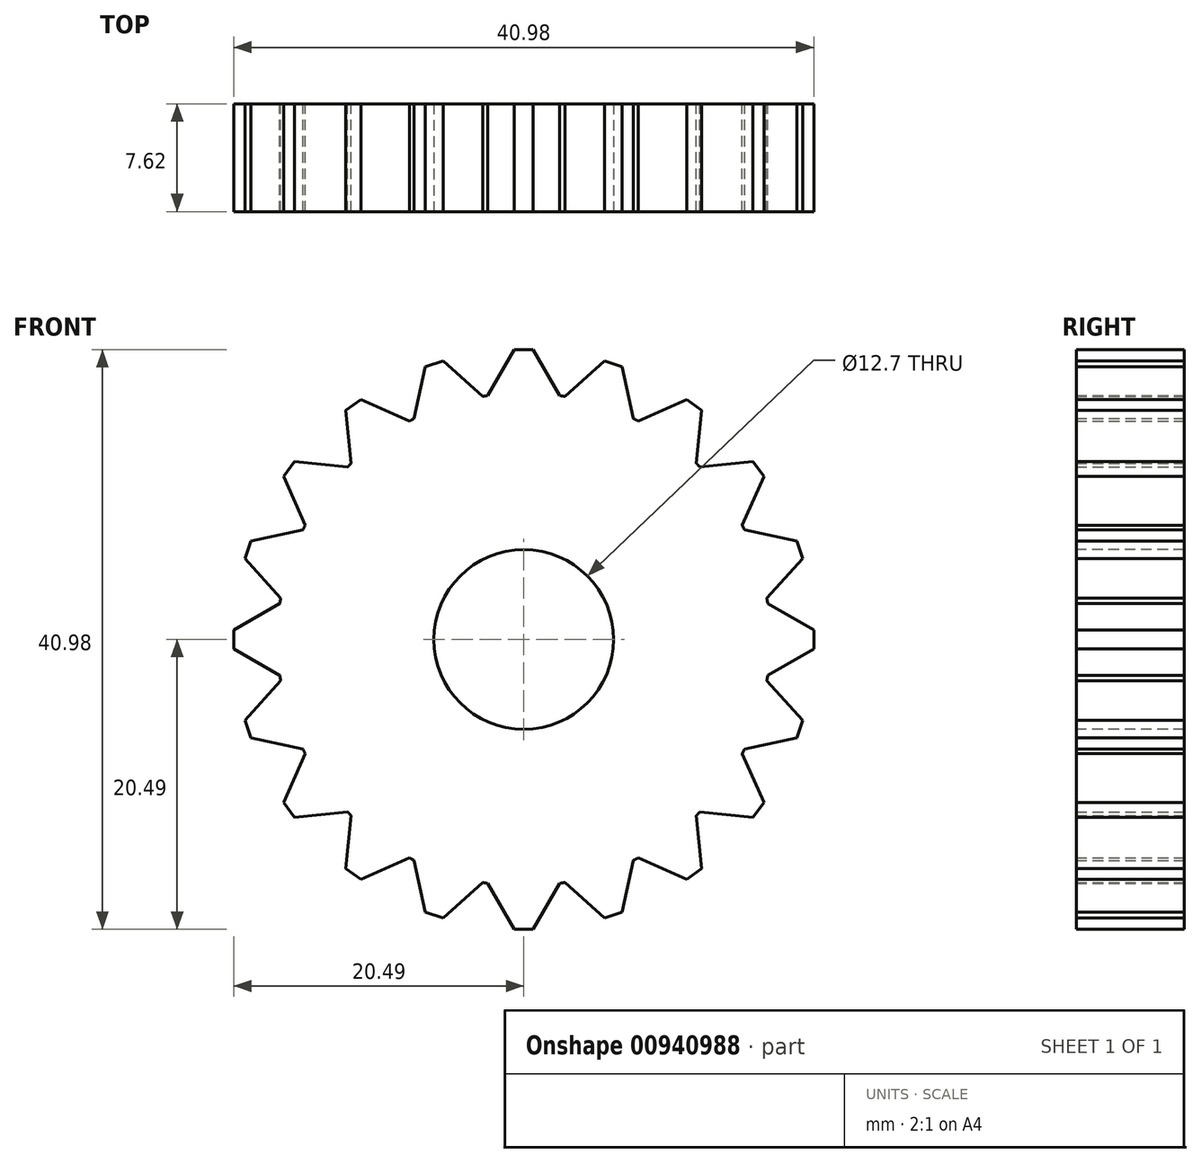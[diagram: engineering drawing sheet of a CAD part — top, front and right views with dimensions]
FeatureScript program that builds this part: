
annotation { "Feature Type Name" : "Feature", "Feature Type Description" : "" }
export const myFeature = defineFeature(function(context is Context, id is Id, definition is map)
    precondition{}
    {
        {
            var Q0;
            Q0=qCreatedBy(makeId("Front.planeOp"),FACE);
            var sketch = newSketch(context, id + "F0", { "sketchPlane" : qUnion([Q0])});
            skCircle(sketch, "E0", {"center": v(0, 0) * mm, "radius": 17.42 * mm});
            skSolve(sketch);
        }
        {
            var Q0;
            Q0=qSketchRegion(id+"F0",true);
            extrude(context, id + "F1", {"entities" : qUnion([Q0]), "depth" : 7.62 * mm, "offsetDistance" : 25.4 * mm});
        }
        {
            var Q0;
            Q0=makeQuery(id+"F1.opExtrude","CAP_FACE",FACE,{"disambiguationData":[OSD([sQuery(id+"F0.wireOp",EDGE,"E0")])],"isStart":true});
            var sketch = newSketch(context, id + "F2", { "sketchPlane" : qUnion([Q0])});
            skCircle(sketch, "E1.cCircle", {"center": v(-18.7, 0) * mm, "radius": 1.47 * mm, "construction": true});
            skLineSegment(sketch, "E1.0", {"start": v(-17.24, 2.54) * mm, "end": v(-17.24, -2.54) * mm});
            skLineSegment(sketch, "E1.1", {"start": v(-17.24, -2.54) * mm, "end": v(-21.63, 0) * mm});
            skLineSegment(sketch, "E1.2", {"start": v(-21.63, 0) * mm, "end": v(-17.24, 2.54) * mm});
            skPoint(sketch, "E1.0.midPoint", {"position": v(-17.24, 0) * mm});
            skLineSegment(sketch, "E2.1.0", {"start": v(-15.6, -7.74) * mm, "end": v(-20.58, -6.69) * mm});
            skLineSegment(sketch, "E2.1.1", {"start": v(-17.18, -2.91) * mm, "end": v(-15.6, -7.74) * mm});
            skLineSegment(sketch, "E2.1.2", {"start": v(-20.58, -6.69) * mm, "end": v(-17.18, -2.91) * mm});
            skLineSegment(sketch, "E2.2.0", {"start": v(-12.45, -12.19) * mm, "end": v(-17.5, -12.72) * mm});
            skLineSegment(sketch, "E2.2.1", {"start": v(-15.44, -8.08) * mm, "end": v(-12.45, -12.19) * mm});
            skLineSegment(sketch, "E2.2.2", {"start": v(-17.5, -12.72) * mm, "end": v(-15.44, -8.08) * mm});
            skPoint(sketch, "E2.center", {"position": v(0, 0) * mm});
            skLineSegment(sketch, "E3.2.3.0", {"start": v(-8.08, -15.44) * mm, "end": v(-12.72, -17.5) * mm});
            skLineSegment(sketch, "E3.3.3.0", {"start": v(-12.19, -12.45) * mm, "end": v(-8.08, -15.44) * mm});
            skLineSegment(sketch, "E3.6.3.0", {"start": v(-12.72, -17.5) * mm, "end": v(-12.19, -12.45) * mm});
            skLineSegment(sketch, "E3.2.4.0", {"start": v(-2.91, -17.18) * mm, "end": v(-6.69, -20.58) * mm});
            skLineSegment(sketch, "E3.3.4.0", {"start": v(-7.74, -15.6) * mm, "end": v(-2.91, -17.18) * mm});
            skLineSegment(sketch, "E3.6.4.0", {"start": v(-6.69, -20.58) * mm, "end": v(-7.74, -15.6) * mm});
            skLineSegment(sketch, "E3.2.5.0", {"start": v(2.54, -17.24) * mm, "end": v(0, -21.63) * mm});
            skLineSegment(sketch, "E3.3.5.0", {"start": v(-2.54, -17.24) * mm, "end": v(2.54, -17.24) * mm});
            skLineSegment(sketch, "E3.6.5.0", {"start": v(0, -21.63) * mm, "end": v(-2.54, -17.24) * mm});
            skLineSegment(sketch, "E3.2.6.0", {"start": v(7.74, -15.6) * mm, "end": v(6.69, -20.58) * mm});
            skLineSegment(sketch, "E3.3.6.0", {"start": v(2.91, -17.18) * mm, "end": v(7.74, -15.6) * mm});
            skLineSegment(sketch, "E3.6.6.0", {"start": v(6.69, -20.58) * mm, "end": v(2.91, -17.18) * mm});
            skLineSegment(sketch, "E3.2.7.0", {"start": v(12.19, -12.45) * mm, "end": v(12.72, -17.5) * mm});
            skLineSegment(sketch, "E3.3.7.0", {"start": v(8.08, -15.44) * mm, "end": v(12.19, -12.45) * mm});
            skLineSegment(sketch, "E3.6.7.0", {"start": v(12.72, -17.5) * mm, "end": v(8.08, -15.44) * mm});
            skLineSegment(sketch, "E3.2.8.0", {"start": v(15.44, -8.08) * mm, "end": v(17.5, -12.72) * mm});
            skLineSegment(sketch, "E3.3.8.0", {"start": v(12.45, -12.19) * mm, "end": v(15.44, -8.08) * mm});
            skLineSegment(sketch, "E3.6.8.0", {"start": v(17.5, -12.72) * mm, "end": v(12.45, -12.19) * mm});
            skLineSegment(sketch, "E4.2.9.0", {"start": v(17.18, -2.91) * mm, "end": v(20.58, -6.69) * mm});
            skLineSegment(sketch, "E4.3.9.0", {"start": v(15.6, -7.74) * mm, "end": v(17.18, -2.91) * mm});
            skLineSegment(sketch, "E4.6.9.0", {"start": v(20.58, -6.69) * mm, "end": v(15.6, -7.74) * mm});
            skLineSegment(sketch, "E4.2.10.0", {"start": v(17.24, 2.54) * mm, "end": v(21.63, 0) * mm});
            skLineSegment(sketch, "E4.3.10.0", {"start": v(17.24, -2.54) * mm, "end": v(17.24, 2.54) * mm});
            skLineSegment(sketch, "E4.6.10.0", {"start": v(21.63, 0) * mm, "end": v(17.24, -2.54) * mm});
            skLineSegment(sketch, "E4.2.11.0", {"start": v(15.6, 7.74) * mm, "end": v(20.58, 6.69) * mm});
            skLineSegment(sketch, "E4.3.11.0", {"start": v(17.18, 2.91) * mm, "end": v(15.6, 7.74) * mm});
            skLineSegment(sketch, "E4.6.11.0", {"start": v(20.58, 6.69) * mm, "end": v(17.18, 2.91) * mm});
            skLineSegment(sketch, "E4.2.12.0", {"start": v(12.45, 12.19) * mm, "end": v(17.5, 12.72) * mm});
            skLineSegment(sketch, "E4.3.12.0", {"start": v(15.44, 8.08) * mm, "end": v(12.45, 12.19) * mm});
            skLineSegment(sketch, "E4.6.12.0", {"start": v(17.5, 12.72) * mm, "end": v(15.44, 8.08) * mm});
            skLineSegment(sketch, "E4.2.13.0", {"start": v(8.08, 15.44) * mm, "end": v(12.72, 17.5) * mm});
            skLineSegment(sketch, "E4.3.13.0", {"start": v(12.19, 12.45) * mm, "end": v(8.08, 15.44) * mm});
            skLineSegment(sketch, "E4.6.13.0", {"start": v(12.72, 17.5) * mm, "end": v(12.19, 12.45) * mm});
            skLineSegment(sketch, "E4.2.14.0", {"start": v(2.91, 17.18) * mm, "end": v(6.69, 20.58) * mm});
            skLineSegment(sketch, "E4.3.14.0", {"start": v(7.74, 15.6) * mm, "end": v(2.91, 17.18) * mm});
            skLineSegment(sketch, "E4.6.14.0", {"start": v(6.69, 20.58) * mm, "end": v(7.74, 15.6) * mm});
            skLineSegment(sketch, "E5.2.15.0", {"start": v(-2.54, 17.24) * mm, "end": v(0, 21.63) * mm});
            skLineSegment(sketch, "E5.3.15.0", {"start": v(2.54, 17.24) * mm, "end": v(-2.54, 17.24) * mm});
            skLineSegment(sketch, "E5.6.15.0", {"start": v(0, 21.63) * mm, "end": v(2.54, 17.24) * mm});
            skLineSegment(sketch, "E6.2.16.0", {"start": v(-7.74, 15.6) * mm, "end": v(-6.69, 20.58) * mm});
            skLineSegment(sketch, "E6.3.16.0", {"start": v(-2.91, 17.18) * mm, "end": v(-7.74, 15.6) * mm});
            skLineSegment(sketch, "E6.6.16.0", {"start": v(-6.69, 20.58) * mm, "end": v(-2.91, 17.18) * mm});
            skLineSegment(sketch, "E6.2.17.0", {"start": v(-12.19, 12.45) * mm, "end": v(-12.72, 17.5) * mm});
            skLineSegment(sketch, "E6.3.17.0", {"start": v(-8.08, 15.44) * mm, "end": v(-12.19, 12.45) * mm});
            skLineSegment(sketch, "E6.6.17.0", {"start": v(-12.72, 17.5) * mm, "end": v(-8.08, 15.44) * mm});
            skLineSegment(sketch, "E7.2.18.0", {"start": v(-15.44, 8.08) * mm, "end": v(-17.5, 12.72) * mm});
            skLineSegment(sketch, "E7.3.18.0", {"start": v(-12.45, 12.19) * mm, "end": v(-15.44, 8.08) * mm});
            skLineSegment(sketch, "E7.6.18.0", {"start": v(-17.5, 12.72) * mm, "end": v(-12.45, 12.19) * mm});
            skLineSegment(sketch, "E7.2.19.0", {"start": v(-17.18, 2.91) * mm, "end": v(-20.58, 6.69) * mm});
            skLineSegment(sketch, "E7.3.19.0", {"start": v(-15.6, 7.74) * mm, "end": v(-17.18, 2.91) * mm});
            skLineSegment(sketch, "E7.6.19.0", {"start": v(-20.58, 6.69) * mm, "end": v(-15.6, 7.74) * mm});
            skSolve(sketch);
        }
        {
            var Q0;
            Q0=qSketchRegion(id+"F2",true);
            var Q1;
            Q1=makeQuery(id+"F1.opExtrude","CAP_FACE",FACE,{"disambiguationData":[OSD([sQuery(id+"F0.wireOp",EDGE,"E0")])],"isStart":false});
            extrude(context, id + "F3", {"entities" : qUnion([Q0]), "operationType" : NewBodyOperationType.ADD, "endBound" : BoundingType.UP_TO_SURFACE, "oppositeDirection" : true, "depth" : 25.4 * mm, "endBoundEntityFace" : qUnion([Q1]), "offsetDistance" : 25.4 * mm});
        }
        {
            var Q0;
            Q0=makeQuery(id+"F3.opExtrude","SWEPT_EDGE",EDGE,{"disambiguationData":[OSD([sQuery(id+"F2.wireOp",EDGE,"E4.2.14.0"),sQuery(id+"F2.wireOp",EDGE,"E4.6.14.0")])]});
            var Q1;
            Q1=makeQuery(id+"F3.opExtrude","SWEPT_EDGE",EDGE,{"disambiguationData":[OSD([sQuery(id+"F2.wireOp",EDGE,"E5.2.15.0"),sQuery(id+"F2.wireOp",EDGE,"E5.6.15.0")])]});
            var Q2;
            Q2=makeQuery(id+"F3.opExtrude","SWEPT_EDGE",EDGE,{"disambiguationData":[OSD([sQuery(id+"F2.wireOp",EDGE,"E6.2.16.0"),sQuery(id+"F2.wireOp",EDGE,"E6.6.16.0")])]});
            var Q3;
            Q3=makeQuery(id+"F3.opExtrude","SWEPT_EDGE",EDGE,{"disambiguationData":[OSD([sQuery(id+"F2.wireOp",EDGE,"E6.2.17.0"),sQuery(id+"F2.wireOp",EDGE,"E6.6.17.0")])]});
            var Q4;
            Q4=makeQuery(id+"F3.opExtrude","SWEPT_EDGE",EDGE,{"disambiguationData":[OSD([sQuery(id+"F2.wireOp",EDGE,"E7.2.18.0"),sQuery(id+"F2.wireOp",EDGE,"E7.6.18.0")])]});
            var Q5;
            Q5=makeQuery(id+"F3.opExtrude","SWEPT_EDGE",EDGE,{"disambiguationData":[OSD([sQuery(id+"F2.wireOp",EDGE,"E7.2.19.0"),sQuery(id+"F2.wireOp",EDGE,"E7.6.19.0")])]});
            var Q6;
            Q6=makeQuery(id+"F3.opExtrude","SWEPT_EDGE",EDGE,{"disambiguationData":[OSD([sQuery(id+"F2.wireOp",EDGE,"E1.1"),sQuery(id+"F2.wireOp",EDGE,"E1.2")])]});
            var Q7;
            Q7=makeQuery(id+"F3.opExtrude","SWEPT_EDGE",EDGE,{"disambiguationData":[OSD([sQuery(id+"F2.wireOp",EDGE,"E2.1.0"),sQuery(id+"F2.wireOp",EDGE,"E2.1.2")])]});
            var Q8;
            Q8=makeQuery(id+"F3.opExtrude","SWEPT_EDGE",EDGE,{"disambiguationData":[OSD([sQuery(id+"F2.wireOp",EDGE,"E4.2.13.0"),sQuery(id+"F2.wireOp",EDGE,"E4.6.13.0")])]});
            var Q9;
            Q9=makeQuery(id+"F3.opExtrude","SWEPT_EDGE",EDGE,{"disambiguationData":[OSD([sQuery(id+"F2.wireOp",EDGE,"E4.2.12.0"),sQuery(id+"F2.wireOp",EDGE,"E4.6.12.0")])]});
            var Q10;
            Q10=makeQuery(id+"F3.opExtrude","SWEPT_EDGE",EDGE,{"disambiguationData":[OSD([sQuery(id+"F2.wireOp",EDGE,"E4.2.11.0"),sQuery(id+"F2.wireOp",EDGE,"E4.6.11.0")])]});
            var Q11;
            Q11=makeQuery(id+"F3.opExtrude","SWEPT_EDGE",EDGE,{"disambiguationData":[OSD([sQuery(id+"F2.wireOp",EDGE,"E4.2.10.0"),sQuery(id+"F2.wireOp",EDGE,"E4.6.10.0")])]});
            var Q12;
            Q12=makeQuery(id+"F3.opExtrude","SWEPT_EDGE",EDGE,{"disambiguationData":[OSD([sQuery(id+"F2.wireOp",EDGE,"E4.2.9.0"),sQuery(id+"F2.wireOp",EDGE,"E4.6.9.0")])]});
            var Q13;
            Q13=makeQuery(id+"F3.opExtrude","SWEPT_EDGE",EDGE,{"disambiguationData":[OSD([sQuery(id+"F2.wireOp",EDGE,"E3.2.8.0"),sQuery(id+"F2.wireOp",EDGE,"E3.6.8.0")])]});
            var Q14;
            Q14=makeQuery(id+"F3.opExtrude","SWEPT_EDGE",EDGE,{"disambiguationData":[OSD([sQuery(id+"F2.wireOp",EDGE,"E3.2.7.0"),sQuery(id+"F2.wireOp",EDGE,"E3.6.7.0")])]});
            var Q15;
            Q15=makeQuery(id+"F3.opExtrude","SWEPT_EDGE",EDGE,{"disambiguationData":[OSD([sQuery(id+"F2.wireOp",EDGE,"E2.2.0"),sQuery(id+"F2.wireOp",EDGE,"E2.2.2")])]});
            var Q16;
            Q16=makeQuery(id+"F3.opExtrude","SWEPT_EDGE",EDGE,{"disambiguationData":[OSD([sQuery(id+"F2.wireOp",EDGE,"E3.2.6.0"),sQuery(id+"F2.wireOp",EDGE,"E3.6.6.0")])]});
            var Q17;
            Q17=makeQuery(id+"F3.opExtrude","SWEPT_EDGE",EDGE,{"disambiguationData":[OSD([sQuery(id+"F2.wireOp",EDGE,"E3.2.5.0"),sQuery(id+"F2.wireOp",EDGE,"E3.6.5.0")])]});
            var Q18;
            Q18=makeQuery(id+"F3.opExtrude","SWEPT_EDGE",EDGE,{"disambiguationData":[OSD([sQuery(id+"F2.wireOp",EDGE,"E3.2.4.0"),sQuery(id+"F2.wireOp",EDGE,"E3.6.4.0")])]});
            var Q19;
            Q19=makeQuery(id+"F3.opExtrude","SWEPT_EDGE",EDGE,{"disambiguationData":[OSD([sQuery(id+"F2.wireOp",EDGE,"E3.2.3.0"),sQuery(id+"F2.wireOp",EDGE,"E3.6.3.0")])]});
            chamfer(context, id + "F4", {"entities" : qUnion([Q0, Q1, Q2, Q3, Q4, Q5, Q6, Q7, Q8, Q9, Q10, Q11, Q12, Q13, Q14, Q15, Q16, Q17, Q18, Q19]), "width" : 0.76 * mm, "tangentPropagation" : true});
        }
        {
            var Q0;
            Q0=makeQuery(id+"F3.boolean.opBoolean","MERGE",FACE,{"derivedFrom":[makeQuery(id+"F1.opExtrude","CAP_FACE",FACE,{"disambiguationData":[OSD([sQuery(id+"F0.wireOp",EDGE,"E0")])],"isStart":false}),makeQuery(id+"F3.opExtrude","CAP_FACE",FACE,{"disambiguationData":[OSD([sQuery(id+"F2.wireOp",EDGE,"E1.0"),sQuery(id+"F2.wireOp",EDGE,"E1.1"),sQuery(id+"F2.wireOp",EDGE,"E1.2")])],"isStart":false}),makeQuery(id+"F3.opExtrude","CAP_FACE",FACE,{"disambiguationData":[OSD([sQuery(id+"F2.wireOp",EDGE,"E2.1.0"),sQuery(id+"F2.wireOp",EDGE,"E2.1.1"),sQuery(id+"F2.wireOp",EDGE,"E2.1.2")])],"isStart":false}),makeQuery(id+"F3.opExtrude","CAP_FACE",FACE,{"disambiguationData":[OSD([sQuery(id+"F2.wireOp",EDGE,"E2.2.0"),sQuery(id+"F2.wireOp",EDGE,"E2.2.1"),sQuery(id+"F2.wireOp",EDGE,"E2.2.2")])],"isStart":false}),makeQuery(id+"F3.opExtrude","CAP_FACE",FACE,{"disambiguationData":[OSD([sQuery(id+"F2.wireOp",EDGE,"E3.2.3.0"),sQuery(id+"F2.wireOp",EDGE,"E3.3.3.0"),sQuery(id+"F2.wireOp",EDGE,"E3.6.3.0")])],"isStart":false}),makeQuery(id+"F3.opExtrude","CAP_FACE",FACE,{"disambiguationData":[OSD([sQuery(id+"F2.wireOp",EDGE,"E3.2.4.0"),sQuery(id+"F2.wireOp",EDGE,"E3.3.4.0"),sQuery(id+"F2.wireOp",EDGE,"E3.6.4.0")])],"isStart":false}),makeQuery(id+"F3.opExtrude","CAP_FACE",FACE,{"disambiguationData":[OSD([sQuery(id+"F2.wireOp",EDGE,"E3.2.5.0"),sQuery(id+"F2.wireOp",EDGE,"E3.3.5.0"),sQuery(id+"F2.wireOp",EDGE,"E3.6.5.0")])],"isStart":false}),makeQuery(id+"F3.opExtrude","CAP_FACE",FACE,{"disambiguationData":[OSD([sQuery(id+"F2.wireOp",EDGE,"E3.2.6.0"),sQuery(id+"F2.wireOp",EDGE,"E3.3.6.0"),sQuery(id+"F2.wireOp",EDGE,"E3.6.6.0")])],"isStart":false}),makeQuery(id+"F3.opExtrude","CAP_FACE",FACE,{"disambiguationData":[OSD([sQuery(id+"F2.wireOp",EDGE,"E3.2.7.0"),sQuery(id+"F2.wireOp",EDGE,"E3.3.7.0"),sQuery(id+"F2.wireOp",EDGE,"E3.6.7.0")])],"isStart":false}),makeQuery(id+"F3.opExtrude","CAP_FACE",FACE,{"disambiguationData":[OSD([sQuery(id+"F2.wireOp",EDGE,"E3.2.8.0"),sQuery(id+"F2.wireOp",EDGE,"E3.3.8.0"),sQuery(id+"F2.wireOp",EDGE,"E3.6.8.0")])],"isStart":false}),makeQuery(id+"F3.opExtrude","CAP_FACE",FACE,{"disambiguationData":[OSD([sQuery(id+"F2.wireOp",EDGE,"E4.2.9.0"),sQuery(id+"F2.wireOp",EDGE,"E4.3.9.0"),sQuery(id+"F2.wireOp",EDGE,"E4.6.9.0")])],"isStart":false}),makeQuery(id+"F3.opExtrude","CAP_FACE",FACE,{"disambiguationData":[OSD([sQuery(id+"F2.wireOp",EDGE,"E4.2.10.0"),sQuery(id+"F2.wireOp",EDGE,"E4.3.10.0"),sQuery(id+"F2.wireOp",EDGE,"E4.6.10.0")])],"isStart":false}),makeQuery(id+"F3.opExtrude","CAP_FACE",FACE,{"disambiguationData":[OSD([sQuery(id+"F2.wireOp",EDGE,"E4.2.11.0"),sQuery(id+"F2.wireOp",EDGE,"E4.3.11.0"),sQuery(id+"F2.wireOp",EDGE,"E4.6.11.0")])],"isStart":false}),makeQuery(id+"F3.opExtrude","CAP_FACE",FACE,{"disambiguationData":[OSD([sQuery(id+"F2.wireOp",EDGE,"E4.2.12.0"),sQuery(id+"F2.wireOp",EDGE,"E4.3.12.0"),sQuery(id+"F2.wireOp",EDGE,"E4.6.12.0")])],"isStart":false}),makeQuery(id+"F3.opExtrude","CAP_FACE",FACE,{"disambiguationData":[OSD([sQuery(id+"F2.wireOp",EDGE,"E4.2.13.0"),sQuery(id+"F2.wireOp",EDGE,"E4.3.13.0"),sQuery(id+"F2.wireOp",EDGE,"E4.6.13.0")])],"isStart":false}),makeQuery(id+"F3.opExtrude","CAP_FACE",FACE,{"disambiguationData":[OSD([sQuery(id+"F2.wireOp",EDGE,"E4.2.14.0"),sQuery(id+"F2.wireOp",EDGE,"E4.3.14.0"),sQuery(id+"F2.wireOp",EDGE,"E4.6.14.0")])],"isStart":false}),makeQuery(id+"F3.opExtrude","CAP_FACE",FACE,{"disambiguationData":[OSD([sQuery(id+"F2.wireOp",EDGE,"E5.2.15.0"),sQuery(id+"F2.wireOp",EDGE,"E5.3.15.0"),sQuery(id+"F2.wireOp",EDGE,"E5.6.15.0")])],"isStart":false}),makeQuery(id+"F3.opExtrude","CAP_FACE",FACE,{"disambiguationData":[OSD([sQuery(id+"F2.wireOp",EDGE,"E6.2.16.0"),sQuery(id+"F2.wireOp",EDGE,"E6.3.16.0"),sQuery(id+"F2.wireOp",EDGE,"E6.6.16.0")])],"isStart":false}),makeQuery(id+"F3.opExtrude","CAP_FACE",FACE,{"disambiguationData":[OSD([sQuery(id+"F2.wireOp",EDGE,"E6.2.17.0"),sQuery(id+"F2.wireOp",EDGE,"E6.3.17.0"),sQuery(id+"F2.wireOp",EDGE,"E6.6.17.0")])],"isStart":false}),makeQuery(id+"F3.opExtrude","CAP_FACE",FACE,{"disambiguationData":[OSD([sQuery(id+"F2.wireOp",EDGE,"E7.2.18.0"),sQuery(id+"F2.wireOp",EDGE,"E7.3.18.0"),sQuery(id+"F2.wireOp",EDGE,"E7.6.18.0")])],"isStart":false}),makeQuery(id+"F3.opExtrude","CAP_FACE",FACE,{"disambiguationData":[OSD([sQuery(id+"F2.wireOp",EDGE,"E7.2.19.0"),sQuery(id+"F2.wireOp",EDGE,"E7.3.19.0"),sQuery(id+"F2.wireOp",EDGE,"E7.6.19.0")])],"isStart":false})]});
            var sketch = newSketch(context, id + "F5", { "sketchPlane" : qUnion([Q0])});
            skCircle(sketch, "E8", {"center": v(0, 0) * mm, "radius": 6.35 * mm});
            skSolve(sketch);
        }
        {
            var Q0;
            Q0=qSketchRegion(id+"F5",true);
            extrude(context, id + "F6", {"entities" : qUnion([Q0]), "operationType" : NewBodyOperationType.REMOVE, "oppositeDirection" : true, "depth" : 25.4 * mm, "offsetDistance" : 25.4 * mm});
        }
    });
